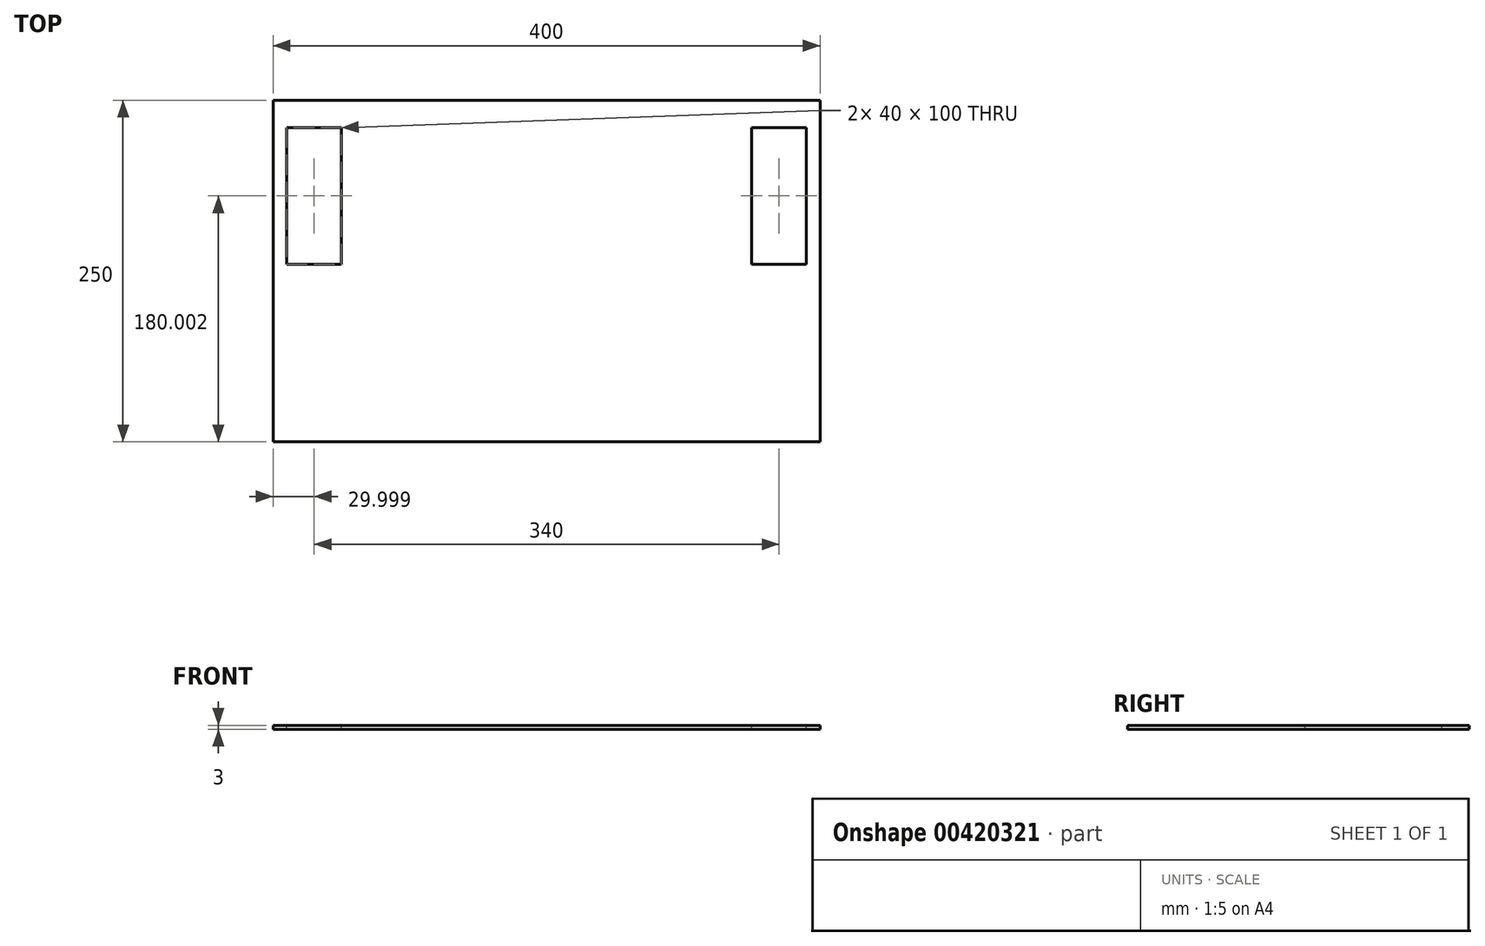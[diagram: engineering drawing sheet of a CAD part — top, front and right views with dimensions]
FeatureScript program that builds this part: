
annotation { "Feature Type Name" : "Feature", "Feature Type Description" : "" }
export const myFeature = defineFeature(function(context is Context, id is Id, definition is map)
    precondition{}
    {
        {
            var Q0;
            Q0=qCreatedBy(makeId("Top.planeOp"),FACE);
            var sketch = newSketch(context, id + "F0", { "sketchPlane" : qUnion([Q0])});
            skLineSegment(sketch, "E0.bottom", {"start": v(-136.2, 111.27) * mm, "end": v(263.8, 111.27) * mm});
            skLineSegment(sketch, "E0.top", {"start": v(-136.2, -138.73) * mm, "end": v(263.8, -138.73) * mm});
            skLineSegment(sketch, "E0.left", {"start": v(-136.2, 111.27) * mm, "end": v(-136.2, -138.73) * mm});
            skLineSegment(sketch, "E0.right", {"start": v(263.8, 111.27) * mm, "end": v(263.8, -138.73) * mm});
            skSolve(sketch);
        }
        {
            var Q0;
            Q0=qSketchRegion(id+"F0",true);
            extrude(context, id + "F1", {"entities" : qUnion([Q0]), "depth" : 3 * mm});
        }
        {
            var Q0;
            Q0=makeQuery(id+"F1.opExtrude","CAP_FACE",FACE,{"disambiguationData":[OSD([sQuery(id+"F0.wireOp",EDGE,"E0.bottom"),sQuery(id+"F0.wireOp",EDGE,"E0.top"),sQuery(id+"F0.wireOp",EDGE,"E0.left"),sQuery(id+"F0.wireOp",EDGE,"E0.right")])],"isStart":false});
            var sketch = newSketch(context, id + "F2", { "sketchPlane" : qUnion([Q0])});
            skLineSegment(sketch, "E1.bottom", {"start": v(-126.2, 91.27) * mm, "end": v(-86.2, 91.27) * mm});
            skLineSegment(sketch, "E1.top", {"start": v(-126.2, -8.73) * mm, "end": v(-86.2, -8.73) * mm});
            skLineSegment(sketch, "E1.left", {"start": v(-126.2, 91.27) * mm, "end": v(-126.2, -8.73) * mm});
            skLineSegment(sketch, "E1.right", {"start": v(-86.2, 91.27) * mm, "end": v(-86.2, -8.73) * mm});
            skLineSegment(sketch, "E2", {"start": v(63.8, 111.27) * mm, "end": v(63.8, -138.73) * mm, "construction": true});
            skLineSegment(sketch, "E3.0.MirrorCS", {"start": v(253.8, 91.27) * mm, "end": v(213.8, 91.27) * mm});
            skLineSegment(sketch, "E4.0.MirrorCS", {"start": v(253.8, 91.27) * mm, "end": v(253.8, -8.73) * mm});
            skLineSegment(sketch, "E5.0.MirrorCS", {"start": v(253.8, -8.73) * mm, "end": v(213.8, -8.73) * mm});
            skLineSegment(sketch, "E6.0.MirrorCS", {"start": v(213.8, 91.27) * mm, "end": v(213.8, -8.73) * mm});
            skSolve(sketch);
        }
        {
            var Q0;
            Q0=qSketchRegion(id+"F2",true);
            extrude(context, id + "F3", {"entities" : qUnion([Q0]), "operationType" : NewBodyOperationType.REMOVE, "endBound" : BoundingType.THROUGH_ALL, "oppositeDirection" : true, "depth" : 25 * mm});
        }
    });
